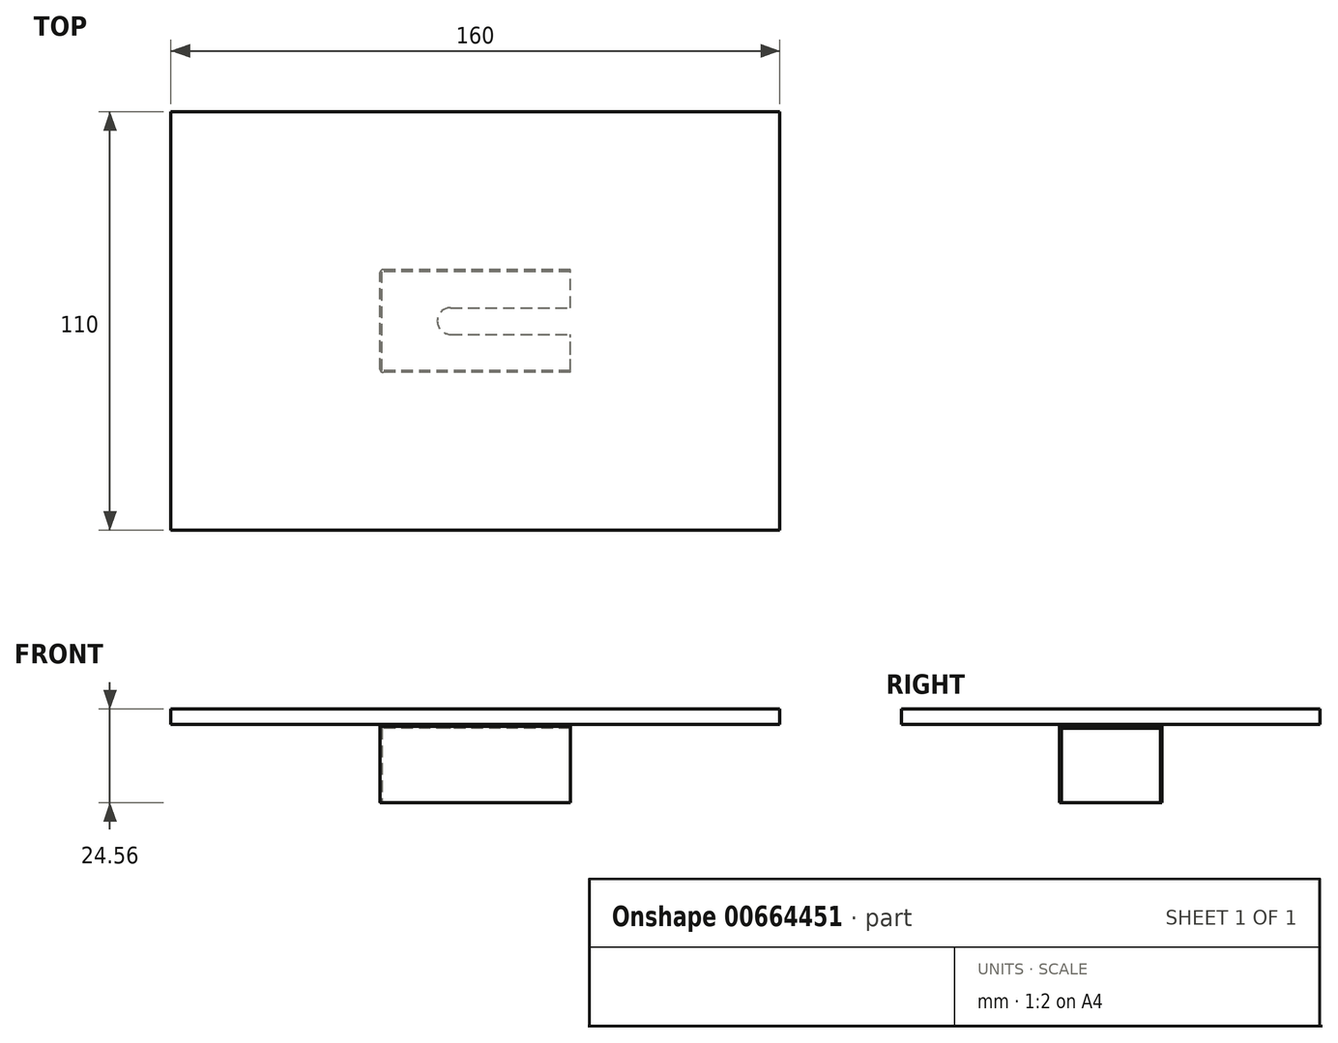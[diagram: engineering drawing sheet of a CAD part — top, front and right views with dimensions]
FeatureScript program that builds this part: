
annotation { "Feature Type Name" : "Feature", "Feature Type Description" : "" }
export const myFeature = defineFeature(function(context is Context, id is Id, definition is map)
    precondition{}
    {
        {
            var Q0;
            Q0=qCreatedBy(makeId("Front.planeOp"),FACE);
            var sketch = newSketch(context, id + "F0", { "sketchPlane" : qUnion([Q0])});
            skLineSegment(sketch, "E0.bottom", {"start": v(25, 10.28) * mm, "end": v(-25, 10.28) * mm});
            skLineSegment(sketch, "E0.top", {"start": v(25, -10.28) * mm, "end": v(-25, -10.28) * mm});
            skLineSegment(sketch, "E0.left", {"start": v(25, 10.28) * mm, "end": v(25, -10.28) * mm});
            skLineSegment(sketch, "E0.right", {"start": v(-25, 10.28) * mm, "end": v(-25, -10.28) * mm});
            skPoint(sketch, "E0.middle", {"position": v(0, 0) * mm});
            skSolve(sketch);
        }
        {
            var Q0;
            Q0=qSketchRegion(id+"F0",true);
            extrude(context, id + "F1", {"entities" : qUnion([Q0]), "depth" : 27 * mm, "offsetDistance" : 25 * mm});
        }
        {
            var Q0;
            Q0=makeQuery(id+"F1.opExtrude","SWEPT_FACE",FACE,{"disambiguationData":[OSD([sQuery(id+"F0.wireOp",EDGE,"E0.left")])]});
            shell(context, id + "F2", {"entities" : qUnion([Q0]), "thickness" : .5 * mm});
        }
        {
            var Q0;
            Q0=makeQuery(id+"F1.opExtrude","SWEPT_FACE",FACE,{"disambiguationData":[OSD([sQuery(id+"F0.wireOp",EDGE,"E0.bottom")])]});
            var sketch = newSketch(context, id + "F3", { "sketchPlane" : qUnion([Q0])});
            skCircle(sketch, "E1", {"center": v(-6.5, -13.5) * mm, "radius": 3.5 * mm});
            skPoint(sketch, "E1.centerSnap0", {"position": v(-25, -13.5) * mm});
            skLineSegment(sketch, "E2", {"start": v(-6.5, -10) * mm, "end": v(25, -10) * mm});
            skLineSegment(sketch, "E3", {"start": v(-6.5, -17) * mm, "end": v(25, -17) * mm});
            skSolve(sketch);
        }
        {
            var Q0;
            Q0=makeQuery(id+"F3.imprint","IMPRINT",FACE,{"disambiguationData":[TD([[makeQuery(id+"F3.imprint","IMPRINT",EDGE,{"derivedFrom":sQuery(id+"F3.wireOp",EDGE,"E1")}),1.0]])]});
            var Q1;
            {var subQ0=sQuery(id+"F3.wireOp",EDGE,"E2");Q1=makeQuery(id+"F3.imprint","IMPRINT",FACE,{"disambiguationData":[TD([[makeQuery(id+"F3.imprint","IMPRINT",EDGE,{"derivedFrom":subQ0}),-1.0]])]});}
            extrude(context, id + "F4", {"entities" : qUnion([Q0, Q1]), "operationType" : NewBodyOperationType.REMOVE, "oppositeDirection" : true, "depth" : 25 * mm, "offsetDistance" : 25 * mm});
        }
        {
            var Q0;
            Q0=makeQuery(id+"F1.opExtrude","SWEPT_FACE",FACE,{"disambiguationData":[OSD([sQuery(id+"F0.wireOp",EDGE,"E0.top")])]});
            var sketch = newSketch(context, id + "F5", { "sketchPlane" : qUnion([Q0])});
            skLineSegment(sketch, "E4.bottom", {"start": v(-25, 27) * mm, "end": v(25, 27) * mm});
            skLineSegment(sketch, "E4.top", {"start": v(-25, 0) * mm, "end": v(25, 0) * mm});
            skLineSegment(sketch, "E4.left", {"start": v(-25, 27) * mm, "end": v(-25, 0) * mm});
            skLineSegment(sketch, "E4.right", {"start": v(25, 27) * mm, "end": v(25, 0) * mm});
            skSolve(sketch);
        }
        {
            var Q0;
            Q0=makeQuery(id+"F5.imprint","IMPRINT",FACE,{"disambiguationData":[TD([[makeQuery(id+"F5.imprint","IMPRINT",EDGE,{"derivedFrom":sQuery(id+"F5.wireOp",EDGE,"E4.bottom")}),1.0]])]});
            extrude(context, id + "F6", {"entities" : qUnion([Q0]), "operationType" : NewBodyOperationType.REMOVE, "oppositeDirection" : true, "depth" : .5 * mm});
        }
        {
            var Q0;
            Q0=makeQuery(id+"F1.opExtrude","SWEPT_FACE",FACE,{"disambiguationData":[OSD([sQuery(id+"F0.wireOp",EDGE,"E0.bottom")])]});
            var sketch = newSketch(context, id + "F7", { "sketchPlane" : qUnion([Q0])});
            skLineSegment(sketch, "E5.0.0", {"start": v(25, 0) * mm, "end": v(-25, 0) * mm});
            skLineSegment(sketch, "E5.0.1", {"start": v(-25, 0) * mm, "end": v(-25, -27) * mm});
            skLineSegment(sketch, "E5.0.2", {"start": v(-25, -27) * mm, "end": v(25, -27) * mm});
            skLineSegment(sketch, "E5.0.3", {"start": v(25, -27) * mm, "end": v(25, 0) * mm});
            skPoint(sketch, "E6.middle.positionSnap0", {"position": v(-25, -13.5) * mm});
            skPoint(sketch, "E6.centerSnap0", {"position": v(-25, -13.5) * mm});
            skLineSegment(sketch, "E7", {"start": v(-6.5, -10) * mm, "end": v(25, -10) * mm});
            skLineSegment(sketch, "E8", {"start": v(-6.5, -17) * mm, "end": v(25, -17) * mm});
            skSolve(sketch);
        }
        {
            var Q0;
            Q0=makeQuery(id+"F7.imprint","IMPRINT",FACE,{"disambiguationData":[TD([[makeQuery(id+"F7.imprint","IMPRINT",EDGE,{"derivedFrom":sQuery(id+"F7.wireOp",EDGE,"E5.0.0")}),1.0]])]});
            extrude(context, id + "F8", {"entities" : qUnion([Q0]), "depth" : .5 * mm});
        }
        {
            var Q0;
            Q0=makeQuery(id+"F1.opExtrude","CAP_EDGE",EDGE,{"disambiguationData":[OSD([sQuery(id+"F0.wireOp",EDGE,"E0.right")])],"isStart":false});
            var Q1;
            Q1=makeQuery(id+"F1.opExtrude","CAP_EDGE",EDGE,{"disambiguationData":[OSD([sQuery(id+"F0.wireOp",EDGE,"E0.right")])],"isStart":true});
            var Q2;
            Q2=makeQuery(id+"F8.opExtrude","SWEPT_EDGE",EDGE,{"disambiguationData":[OSD([sQuery(id+"F7.wireOp",EDGE,"E5.0.1"),sQuery(id+"F7.wireOp",EDGE,"E5.0.2")])]});
            var Q3;
            Q3=makeQuery(id+"F8.opExtrude","SWEPT_EDGE",EDGE,{"disambiguationData":[OSD([sQuery(id+"F7.wireOp",EDGE,"E5.0.0"),sQuery(id+"F7.wireOp",EDGE,"E5.0.1")])]});
            fillet(context, id + "F9", {"entities" : qUnion([Q0, Q1, Q2, Q3]), "radius" : .8 * mm, "allowEdgeOverflow" : false});
        }
        {
            var Q0;
            Q0=makeQuery(id+"F8.opExtrude","CAP_FACE",FACE,{"disambiguationData":[OSD([sQuery(id+"F3.wireOp",EDGE,"E1"),sQuery(id+"F7.wireOp",EDGE,"E5.0.0"),sQuery(id+"F7.wireOp",EDGE,"E5.0.1"),sQuery(id+"F7.wireOp",EDGE,"E5.0.2"),sQuery(id+"F7.wireOp",EDGE,"E5.0.3"),sQuery(id+"F7.wireOp",EDGE,"E7"),sQuery(id+"F7.wireOp",EDGE,"E8")])],"isStart":false});
            var sketch = newSketch(context, id + "F10", { "sketchPlane" : qUnion([Q0])});
            skLineSegment(sketch, "E9.bottom", {"start": v(80, -68.5) * mm, "end": v(-80, -68.5) * mm});
            skLineSegment(sketch, "E9.top", {"start": v(80, 41.5) * mm, "end": v(-80, 41.5) * mm});
            skLineSegment(sketch, "E9.left", {"start": v(80, -68.5) * mm, "end": v(80, 41.5) * mm});
            skLineSegment(sketch, "E9.right", {"start": v(-80, -68.5) * mm, "end": v(-80, 41.5) * mm});
            skPoint(sketch, "E9.middle", {"position": v(0, -13.5) * mm});
            skPoint(sketch, "E9.middle.positionSnap0", {"position": v(-25, -13.5) * mm});
            skPoint(sketch, "E9.centerSnap0", {"position": v(-25, -13.5) * mm});
            skSolve(sketch);
        }
        {
            var Q0;
            Q0=makeQuery(id+"F10.imprint","IMPRINT",FACE,{"disambiguationData":[TD([[makeQuery(id+"F10.imprint","IMPRINT",EDGE,{"derivedFrom":sQuery(id+"F10.wireOp",EDGE,"E9.bottom")}),-1.0]])]});
            var Q1;
            {var subQ1=sQuery(id+"F7.wireOp",EDGE,"E7");Q1=makeQuery(id+"F10.imprint","IMPRINT",FACE,{"disambiguationData":[TD([[makeQuery(id+"F10.imprint","IMPRINT",EDGE,{"derivedFrom":makeQuery(id+"F8.opExtrude","CAP_EDGE",EDGE,{"disambiguationData":[OSD([subQ1])],"isStart":false})}),1.0]])]});}
            extrude(context, id + "F11", {"entities" : qUnion([Q0, Q1]), "depth" : 4 * mm, "offsetDistance" : 25 * mm});
        }
    });
